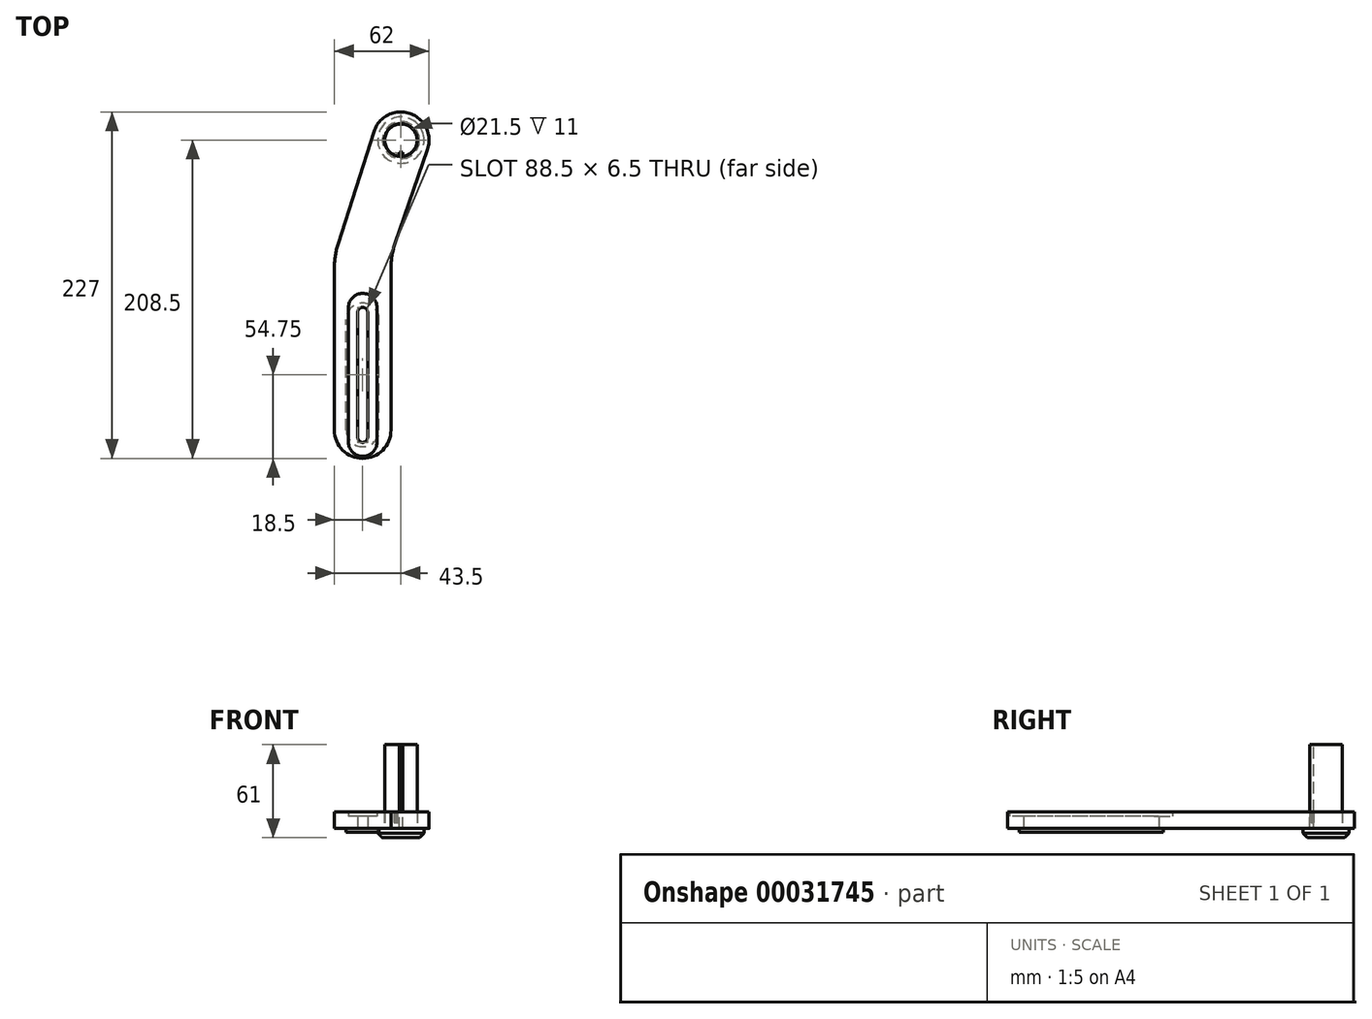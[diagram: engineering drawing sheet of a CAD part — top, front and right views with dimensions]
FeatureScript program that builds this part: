
annotation { "Feature Type Name" : "Feature", "Feature Type Description" : "" }
export const myFeature = defineFeature(function(context is Context, id is Id, definition is map)
    precondition{}
    {
        {
            var Q0;
            Q0=qCreatedBy(makeId("Top.planeOp"),FACE);
            var sketch = newSketch(context, id + "F0", { "sketchPlane" : qUnion([Q0])});
            skLineSegment(sketch, "E0.left", {"start": v(0, 0) * mm, "end": v(0, 114.5) * mm});
            skLineSegment(sketch, "E0.right", {"start": v(37, 0) * mm, "end": v(37, 114.5) * mm});
            skArc(sketch, "E1", {"start": v(0, 0) * mm, "mid": v(18.5, -18.5) * mm, "end": v(37, 0) * mm});
            skCircle(sketch, "E2", {"center": v(43.5, 190) * mm, "radius": 10.75 * mm});
            skArc(sketch, "E3", {"start": v(60.99, 183.96) * mm, "mid": v(49.33, 207.56) * mm, "end": v(25.87, 195.62) * mm});
            skLineSegment(sketch, "E4", {"start": v(0, 114.5) * mm, "end": v(25.87, 195.62) * mm});
            skLineSegment(sketch, "E5", {"start": v(37, 114.5) * mm, "end": v(60.99, 183.96) * mm});
            skSolve(sketch);
        }
        {
            var Q0;
            Q0 = qSketchRegion(id + "F0", true);
            extrude(context, id + "F1", {"entities" : qUnion([Q0]), "depth" : 8 * mm});
        }
        {
            var Q0;
            Q0=makeQuery(id+"F1.opExtrude","CAP_FACE",FACE,{"disambiguationData":[OSD([sQuery(id+"F0.wireOp",EDGE,"E0.left"),sQuery(id+"F0.wireOp",EDGE,"E0.right"),sQuery(id+"F0.wireOp",EDGE,"E1"),sQuery(id+"F0.wireOp",EDGE,"17b39365-8552-41ff-bf17-2f0143301558"),sQuery(id+"F0.wireOp",EDGE,"c914b5d8-53f2-4ac4-93b2-2ecc952be14a")])],"isStart":true});
            var sketch = newSketch(context, id + "F2", { "sketchPlane" : qUnion([Q0])});
            skLineSegment(sketch, "E6.left", {"start": v(7.7, 0) * mm, "end": v(7.7, -72.5) * mm});
            skLineSegment(sketch, "E6.right", {"start": v(29.3, 0) * mm, "end": v(29.3, -72.5) * mm});
            skLineSegment(sketch, "E7", {"start": v(18.5, 153.67) * mm, "end": v(18.5, -165.42) * mm, "construction": true});
            skArc(sketch, "E8", {"start": v(29.3, 0) * mm, "mid": v(18.5, 10.8) * mm, "end": v(7.7, 0) * mm});
            skArc(sketch, "E9", {"start": v(7.7, -72.5) * mm, "mid": v(18.5, -83.3) * mm, "end": v(29.3, -72.5) * mm});
            skSolve(sketch);
        }
        {
            var Q0;
            Q0 = qSketchRegion(id + "F2", true);
            extrude(context, id + "F3", {"entities" : qUnion([Q0]), "operationType" : NewBodyOperationType.ADD, "depth" : 2.5 * mm});
        }
        {
            var Q0;
            Q0=makeQuery(id+"F3.opExtrude","CAP_FACE",FACE,{"disambiguationData":[OSD([sQuery(id+"F2.wireOp",EDGE,"E6.left"),sQuery(id+"F2.wireOp",EDGE,"E6.right"),sQuery(id+"F2.wireOp",EDGE,"E8"),sQuery(id+"F2.wireOp",EDGE,"E9")])],"isStart":false});
            var sketch = newSketch(context, id + "F4", { "sketchPlane" : qUnion([Q0])});
            skLineSegment(sketch, "E10.left", {"start": v(15.25, 4.75) * mm, "end": v(15.25, -77.25) * mm});
            skLineSegment(sketch, "E10.right", {"start": v(21.75, 4.75) * mm, "end": v(21.75, -77.25) * mm});
            skArc(sketch, "E11", {"start": v(21.75, 4.75) * mm, "mid": v(18.5, 8) * mm, "end": v(15.25, 4.75) * mm});
            skArc(sketch, "E12", {"start": v(15.25, -77.25) * mm, "mid": v(18.5, -80.5) * mm, "end": v(21.75, -77.25) * mm});
            skPoint(sketch, "E13", {"position": v(18.5, 10.8) * mm});
            skLineSegment(sketch, "E14", {"start": v(-85.18, -36.25) * mm, "end": v(153.6, -36.25) * mm, "construction": true});
            skSolve(sketch);
        }
        {
            var Q0;
            Q0 = qSketchRegion(id + "F4", true);
            extrude(context, id + "F5", {"entities" : qUnion([Q0]), "operationType" : NewBodyOperationType.REMOVE, "oppositeDirection" : true, "depth" : 25 * mm});
        }
        {
            var Q0;
            Q0=makeQuery(id+"F1.opExtrude","CAP_FACE",FACE,{"disambiguationData":[OSD([sQuery(id+"F0.wireOp",EDGE,"E0.left"),sQuery(id+"F0.wireOp",EDGE,"E0.right"),sQuery(id+"F0.wireOp",EDGE,"E1"),sQuery(id+"F0.wireOp",EDGE,"E2"),sQuery(id+"F0.wireOp",EDGE,"E3"),sQuery(id+"F0.wireOp",EDGE,"E4"),sQuery(id+"F0.wireOp",EDGE,"E5")])],"isStart":false});
            var sketch = newSketch(context, id + "F6", { "sketchPlane" : qUnion([Q0])});
            skLineSegment(sketch, "E15.left", {"start": v(9.15, 80.28) * mm, "end": v(9.15, -7.75) * mm});
            skArc(sketch, "E16", {"start": v(9.15, -7.75) * mm, "mid": v(18.5, -17.1) * mm, "end": v(27.85, -7.75) * mm});
            skLineSegment(sketch, "E15.right", {"start": v(27.85, 80.28) * mm, "end": v(27.85, -7.75) * mm});
            skArc(sketch, "E17", {"start": v(27.85, 80.28) * mm, "mid": v(18.5, 89.63) * mm, "end": v(9.15, 80.28) * mm});
            skLineSegment(sketch, "E18", {"start": v(18.5, 29.39) * mm, "end": v(18.5, 67.53) * mm, "construction": true});
            skPoint(sketch, "E18.startSnap0", {"position": v(18.5, 80.5) * mm});
            skLineSegment(sketch, "E19.0", {"start": v(0, 114.5) * mm, "end": v(25.87, 195.62) * mm});
            skLineSegment(sketch, "E19.1", {"start": v(0, 0) * mm, "end": v(0, 114.5) * mm});
            skArc(sketch, "E19.2", {"start": v(0, 0) * mm, "mid": v(18.5, -18.5) * mm, "end": v(37, 0) * mm});
            skLineSegment(sketch, "E19.3", {"start": v(37, 0) * mm, "end": v(37, 114.5) * mm});
            skLineSegment(sketch, "E19.4", {"start": v(37, 114.5) * mm, "end": v(60.99, 183.96) * mm});
            skArc(sketch, "E19.5", {"start": v(60.99, 183.96) * mm, "mid": v(49.33, 207.56) * mm, "end": v(25.87, 195.62) * mm});
            skCircle(sketch, "E20.0", {"center": v(43.5, 190) * mm, "radius": 10.75 * mm});
            skSolve(sketch);
        }
        {
            var Q0;
            Q0 = qSketchRegion(id + "F6", true);
            extrude(context, id + "F7", {"entities" : qUnion([Q0]), "operationType" : NewBodyOperationType.ADD, "depth" : 3 * mm});
        }
        {
            var Q0;
            Q0=makeQuery(id+"F7.opExtrude","CAP_FACE",FACE,{"disambiguationData":[OSD([sQuery(id+"F6.wireOp",EDGE,"E15.left"),sQuery(id+"F6.wireOp",EDGE,"E16"),sQuery(id+"F6.wireOp",EDGE,"E15.right"),sQuery(id+"F6.wireOp",EDGE,"E17"),sQuery(id+"F6.wireOp",EDGE,"E19.0"),sQuery(id+"F6.wireOp",EDGE,"E19.1"),sQuery(id+"F6.wireOp",EDGE,"E19.2"),sQuery(id+"F6.wireOp",EDGE,"E19.3"),sQuery(id+"F6.wireOp",EDGE,"E19.4"),sQuery(id+"F6.wireOp",EDGE,"E19.5"),sQuery(id+"F6.wireOp",EDGE,"E20.0")])],"isStart":false});
            var sketch = newSketch(context, id + "F8", { "sketchPlane" : qUnion([Q0])});
            skLineSegment(sketch, "E21", {"start": v(43.5, 190) * mm, "end": v(32.9, 159.27) * mm, "construction": true});
            skLineSegment(sketch, "E22", {"start": v(39.06, 180.2) * mm, "end": v(39.71, 182.1) * mm});
            skLineSegment(sketch, "E23", {"start": v(39.71, 182.1) * mm, "end": v(41.6, 181.45) * mm});
            skLineSegment(sketch, "E24", {"start": v(41.6, 181.45) * mm, "end": v(40.95, 179.56) * mm});
            skArc(sketch, "E25", {"start": v(39.06, 180.2) * mm, "mid": v(40, 179.84) * mm, "end": v(40.95, 179.56) * mm});
            skSolve(sketch);
        }
        {
            var Q0;
            {var subQ1=sQuery(id+"F8.wireOp",EDGE,"E25");Q0=makeQuery(id+"F8.imprint","IMPRINT",FACE,{"disambiguationData":[TD([[makeQuery(id+"F8.imprint","IMPRINT",EDGE,{"derivedFrom":subQ1}),1.0]])]});}
            var Q1;
            {var subQ3=sQuery(id+"F8.wireOp",EDGE,"E22");Q1=makeQuery(id+"F8.imprint","IMPRINT",FACE,{"disambiguationData":[TD([[makeQuery(id+"F8.imprint","IMPRINT",EDGE,{"derivedFrom":subQ3}),-1.0]])]});}
            extrude(context, id + "F9", {"entities" : qUnion([Q0, Q1]), "operationType" : NewBodyOperationType.ADD, "oppositeDirection" : true, "depth" : 7 * mm});
        }
        {
            var Q0;
            Q0=makeQuery(id+"F7.boolean.opBoolean","MERGE",EDGE,{"derivedFrom":[makeQuery(id+"F1.opExtrude","SWEPT_EDGE",EDGE,{"disambiguationData":[OSD([sQuery(id+"F0.wireOp",EDGE,"E0.left"),sQuery(id+"F0.wireOp",EDGE,"E4")])]}),makeQuery(id+"F7.opExtrude","SWEPT_EDGE",EDGE,{"disambiguationData":[OSD([sQuery(id+"F6.wireOp",EDGE,"E19.0"),sQuery(id+"F6.wireOp",EDGE,"E19.1")])]})]});
            var Q1;
            Q1=makeQuery(id+"F7.boolean.opBoolean","MERGE",EDGE,{"derivedFrom":[makeQuery(id+"F1.opExtrude","SWEPT_EDGE",EDGE,{"disambiguationData":[OSD([sQuery(id+"F0.wireOp",EDGE,"E0.right"),sQuery(id+"F0.wireOp",EDGE,"E5")])]}),makeQuery(id+"F7.opExtrude","SWEPT_EDGE",EDGE,{"disambiguationData":[OSD([sQuery(id+"F6.wireOp",EDGE,"E19.3"),sQuery(id+"F6.wireOp",EDGE,"E19.4")])]})]});
            fillet(context, id + "F10", {"entities" : qUnion([Q0, Q1]), "radius" : 50 * mm, "tangentPropagation" : true, "allowEdgeOverflow" : false});
        }
        {
            var Q0;
            Q0=makeQuery(id+"F1.opExtrude","CAP_FACE",FACE,{"disambiguationData":[OSD([sQuery(id+"F0.wireOp",EDGE,"E0.left"),sQuery(id+"F0.wireOp",EDGE,"E0.right"),sQuery(id+"F0.wireOp",EDGE,"E1"),sQuery(id+"F0.wireOp",EDGE,"E2"),sQuery(id+"F0.wireOp",EDGE,"E3"),sQuery(id+"F0.wireOp",EDGE,"E4"),sQuery(id+"F0.wireOp",EDGE,"E5")])],"isStart":true});
            var sketch = newSketch(context, id + "F11", { "sketchPlane" : qUnion([Q0])});
            skCircle(sketch, "E26", {"center": v(43.5, -190) * mm, "radius": 10.6 * mm});
            skSolve(sketch);
        }
        {
            var Q0;
            Q0=makeQuery(id+"F11.imprint","IMPRINT",FACE,{"disambiguationData":[TD([[makeQuery(id+"F11.imprint","IMPRINT",EDGE,{"derivedFrom":sQuery(id+"F11.wireOp",EDGE,"E26")}),1.0]])]});
            extrude(context, id + "F12", {"entities" : qUnion([Q0]), "oppositeDirection" : true, "depth" : 55 * mm});
        }
        {
            var Q0;
            Q0=makeQuery(id+"F12.opExtrude","CAP_FACE",FACE,{"disambiguationData":[OSD([sQuery(id+"F11.wireOp",EDGE,"E26")])],"isStart":true});
            var sketch = newSketch(context, id + "F13", { "sketchPlane" : qUnion([Q0])});
            skCircle(sketch, "E27", {"center": v(43.5, -190) * mm, "radius": 15.15 * mm});
            skSolve(sketch);
        }
        {
            var Q0;
            Q0 = qSketchRegion(id + "F13", true);
            extrude(context, id + "F14", {"entities" : qUnion([Q0]), "depth" : 6 * mm});
        }
        {
            var Q0;
            Q0=makeQuery(id+"F14.opExtrude","CAP_EDGE",EDGE,{"disambiguationData":[OSD([sQuery(id+"F13.wireOp",EDGE,"E27")])],"isStart":false});
            chamfer(context, id + "F15", {"entities" : qUnion([Q0]), "width" : 3 * mm, "tangentPropagation" : true});
        }
        {
            var Q0;
            Q0=makeQuery(id+"F12.opExtrude","CAP_FACE",FACE,{"disambiguationData":[OSD([sQuery(id+"F11.wireOp",EDGE,"E26")])],"isStart":false});
            var sketch = newSketch(context, id + "F16", { "sketchPlane" : qUnion([Q0])});
            skLineSegment(sketch, "E28", {"start": v(43.5, 190) * mm, "end": v(43.5, 176.18) * mm, "construction": true});
            skLineSegment(sketch, "E29.top", {"start": v(42.4, 181.96) * mm, "end": v(44.6, 181.96) * mm});
            skLineSegment(sketch, "E29.left", {"start": v(42.4, 179.46) * mm, "end": v(42.4, 181.96) * mm});
            skLineSegment(sketch, "E29.right", {"start": v(44.6, 179.46) * mm, "end": v(44.6, 181.96) * mm});
            skArc(sketch, "E30", {"start": v(42.4, 179.46) * mm, "mid": v(43.5, 179.4) * mm, "end": v(44.6, 179.46) * mm});
            skSolve(sketch);
        }
        {
            var Q0;
            Q0=makeQuery(id+"F16.imprint","IMPRINT",FACE,{"disambiguationData":[TD([[makeQuery(id+"F16.imprint","IMPRINT",EDGE,{"derivedFrom":sQuery(id+"F16.wireOp",EDGE,"E29.top")}),-1.0]])]});
            extrude(context, id + "F17", {"entities" : qUnion([Q0]), "operationType" : NewBodyOperationType.REMOVE, "oppositeDirection" : true, "depth" : 55 * mm});
        }
    });
